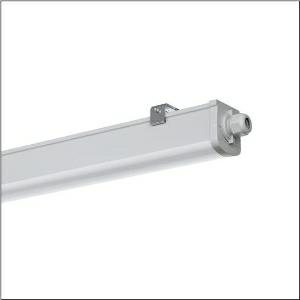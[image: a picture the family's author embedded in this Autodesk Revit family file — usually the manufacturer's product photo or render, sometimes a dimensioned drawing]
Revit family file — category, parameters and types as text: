
# Revit family: monsun_r__31_51fa207d420b_180d
name_source: partatom
category: Lighting Fixtures
units: mm (PartAtom-declared; Revit-internal decimal feet)

## family parameters
Cut with Voids When Loaded = No
Host = Face
Light Source = No
Part Type = Normal
Room Calculation Point = No
Round Connector Dimension = Use Diameter
Shared = No

## types (1)
- Monsun® 31 (1 x LED, 2300 lm, 19 W, 4000K)
    Apparent Load = 19 VA
    CIE Flux Codes = 42 72 91 92 100
    Color Rendering = 80
    Color Temperature = 4000K
    Default Elevation = 1800 mm
    Description = Monsun® 31, damp-proof luminaire, primary optical cover: diffuser, of PC, frosted, light emission: direct distribution, primary light characteristic: symmetric, installation type: surface-mounted, LED, rated luminous flux: 2.300lm, luminous efficacy: 121lm/W, light colour: 840, colour temperature: 4000K, control gear: ON/OFF, with terminal, 3+1-pole, max. 2.5mm², through-wiring: 3x 2.5mm² + 1x 1.5mm², mains connection: 220..240V, AC, 50/60Hz, rated input power: 19W, housing, luminaire housing, of PC, light grey (RAL 7035), length: 558mm, width: 68mm, height: 76mm, protection rating (complete): IP66, insulation class (complete): insulation class II (safety insulation), certification: CE, ENEC, UKCA, protection symbol: D, impact resistance: IK08, permissible operating ambient temperature: -20..+40°C, corresponds to IFS (International Featured Standards) requirements for safety and quality in the food industry, contact your sales advisor before using the luminaires in applications with unclear chemical exposure, large temperature fluctuations or condensation-forming humidity, packaging unit: 1 piece
    Height = 77 mm
    Lamp = 1 x LED
    Lamp Light Flux = 2300 lm
    Lamp Power = 19 W
    Lamp count = 1
    Length = 618 mm
    Luminous efficacy = 121 lm/W
    Manufacturer = Siteco
    ModVariant = No
    Model = 51FA207D420B
    Mounting Place = Ceiling
    Mounting Type = Surface mounted
    Number of Poles = 1
    OnlyDefault = Yes
    Power Factor = 1
    Product Name = Monsun® 31
    Product group = damp-proof luminaire
    ProductGroupID = 300
    Protection Class = Protection class II
    Protection Degree = IP 66
    RLX_Detail_Level = 1
    RLX_Emergency_Light_Flux = 0 lm
    RLX_Emergency_Type = 0
    RLX_Emergency_Type_DB = No
    RlxData = <blob elided: 32961 chars, md5=ab34227f>
    Socket = socket
    Standby Power = 0 W
    System Light Flux = 2300 lm
    System Power = 19 W
    Type Comments = Product without accessories
    Type Image = l_1006174.jpg
    URL = http://relux.com
    VarID = ---
    Voltage = 0 V
    Weight = 0.00 kg
    Width = 69 mm

## geometry (parser evidence)
native form markers: Blend x4, Sweep x11
no freeform markers — native parametric forms only
